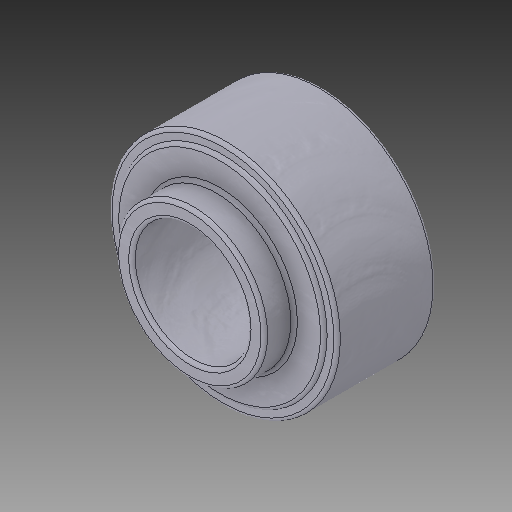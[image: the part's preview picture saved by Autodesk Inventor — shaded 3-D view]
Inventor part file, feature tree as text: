
AUTODESK INVENTOR PART (.ipt)
format: ipt  version: 2019 (Build 230136000, 136)  size: 223,744 bytes
history: native  units: in
note: dims shown in document units (in); Inventor stores cm internally (conversion verified against a paired STEP export)
features: sketch x6, other x3
ambient origin geometry x8: Origin, YZ Plane, XZ Plane, XY Plane, X Axis, Y Axis, Z Axis, Center Point
bodies: Solid1 (feature_tree)
feature tree (9):
  other  "project flange bearing part2_MIR1.ipt"
  other  "Solid1::project flange bearing part2_MIR1.ipt"
  other  "TaggingFeature1"
  sketch  "Sketch1"  dims[d0=0.3937in]
  sketch  "Sketch2"
  sketch  "Sketch3"
  sketch  "Sketch4"
  sketch  "Sketch5"
  sketch  "Sketch6"
